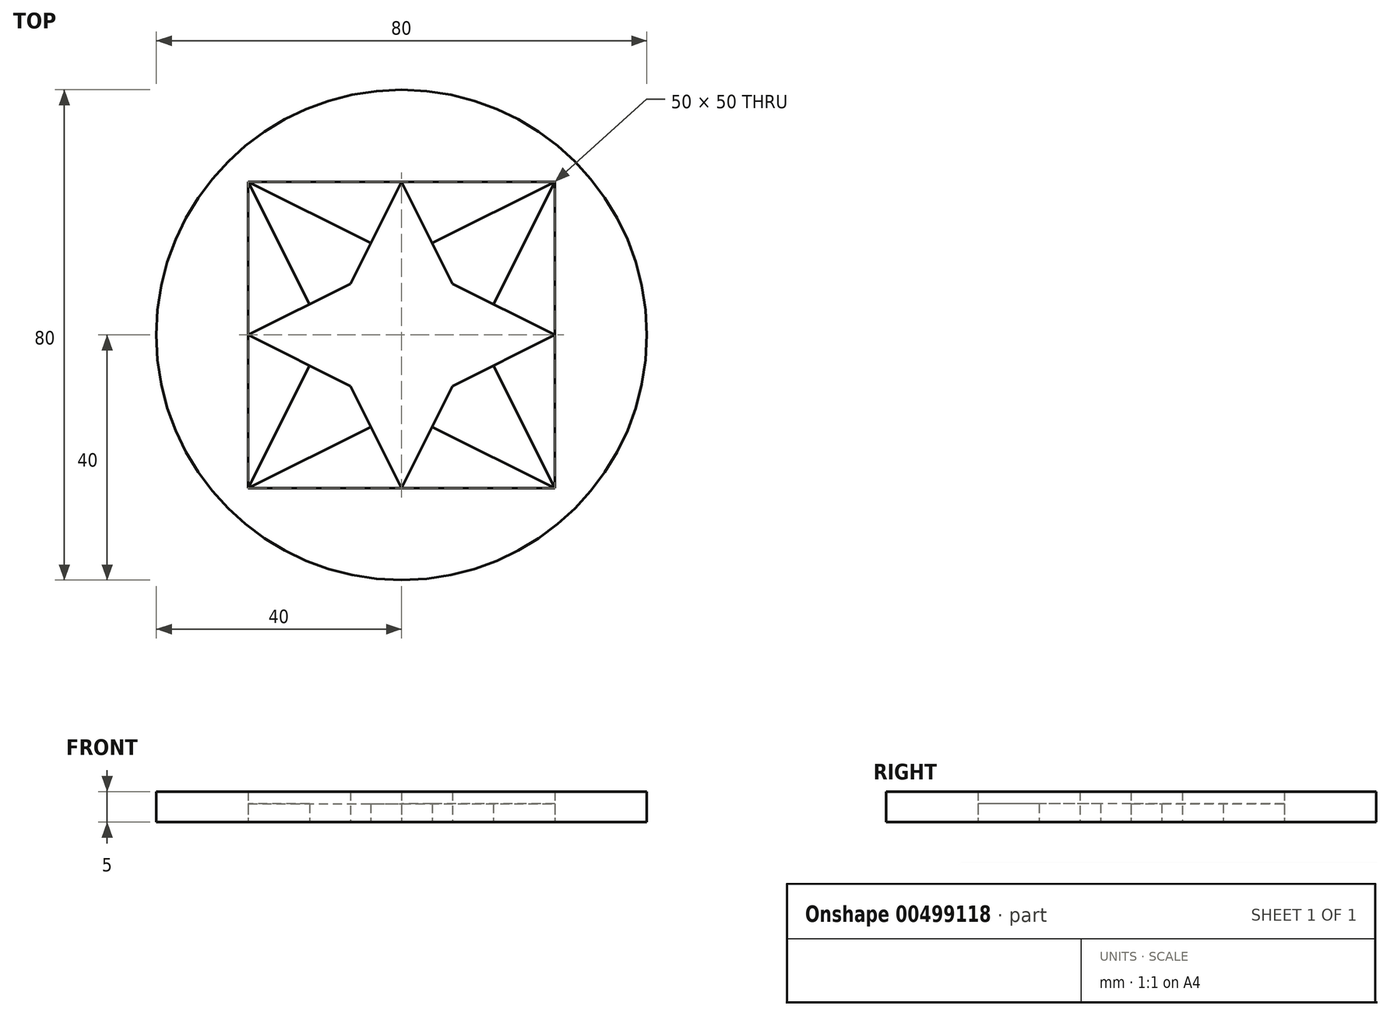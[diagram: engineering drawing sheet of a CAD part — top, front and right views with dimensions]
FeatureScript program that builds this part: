
annotation { "Feature Type Name" : "Feature", "Feature Type Description" : "" }
export const myFeature = defineFeature(function(context is Context, id is Id, definition is map)
    precondition{}
    {
        {
            var Q0;
            Q0=qCreatedBy(makeId("Top.planeOp"),FACE);
            var sketch = newSketch(context, id + "F0", { "sketchPlane" : qUnion([Q0])});
            skCircle(sketch, "E0", {"center": v(0, 0) * mm, "radius": 40 * mm});
            skLineSegment(sketch, "E1.bottom", {"start": v(-25, 25) * mm, "end": v(25, 25) * mm});
            skLineSegment(sketch, "E1.top", {"start": v(-25, -25) * mm, "end": v(25, -25) * mm});
            skLineSegment(sketch, "E1.left", {"start": v(-25, 25) * mm, "end": v(-25, -25) * mm});
            skLineSegment(sketch, "E1.right", {"start": v(25, 25) * mm, "end": v(25, -25) * mm});
            skLineSegment(sketch, "E2", {"start": v(-25, 25) * mm, "end": v(25, 0) * mm});
            skLineSegment(sketch, "E3", {"start": v(25, 0) * mm, "end": v(-25, -25) * mm});
            skLineSegment(sketch, "E4", {"start": v(-25, -25) * mm, "end": v(0, 25) * mm});
            skLineSegment(sketch, "E5", {"start": v(0, 25) * mm, "end": v(25, -25) * mm});
            skLineSegment(sketch, "E6", {"start": v(25, -25) * mm, "end": v(-25, 0) * mm});
            skLineSegment(sketch, "E7", {"start": v(-25, 0) * mm, "end": v(25, 25) * mm});
            skLineSegment(sketch, "E8", {"start": v(25, 25) * mm, "end": v(0, -25) * mm});
            skLineSegment(sketch, "E9", {"start": v(0, -25) * mm, "end": v(-25, 25) * mm});
            skSolve(sketch);
        }
        {
            var Q0;
            Q0=makeQuery(id+"F0.imprint","IMPRINT",FACE,{"disambiguationData":[TD([[makeQuery(id+"F0.imprint","IMPRINT",EDGE,{"derivedFrom":sQuery(id+"F0.wireOp",EDGE,"E0")}),1.0]])]});
            var Q1;
            {var subQ0=sQuery(id+"F0.wireOp",EDGE,"E6");var subQ1=sQuery(id+"F0.wireOp",EDGE,"E4");var subQ2=makeQuery(id+"F0.imprint","INTERSECT",VERTEX,{"derivedFrom":[subQ1,subQ0]});Q1=makeQuery(id+"F0.imprint","IMPRINT",FACE,{"disambiguationData":[TD([[makeQuery(id+"F0.imprint","IMPRINT",EDGE,{"disambiguationData":[TD([[subQ2,-1.0]])],"derivedFrom":subQ1}),1.0]])]});}
            var Q2;
            {var subQ0=sQuery(id+"F0.wireOp",EDGE,"E3");var subQ5=sQuery(id+"F0.wireOp",EDGE,"E5");var subQ6=makeQuery(id+"F0.imprint","INTERSECT",VERTEX,{"derivedFrom":[subQ0,subQ5]});Q2=makeQuery(id+"F0.imprint","IMPRINT",FACE,{"disambiguationData":[TD([[makeQuery(id+"F0.imprint","IMPRINT",EDGE,{"disambiguationData":[TD([[subQ6,1.0]])],"derivedFrom":subQ5}),1.0]])]});}
            var Q3;
            {var subQ0=sQuery(id+"F0.wireOp",EDGE,"E4");var subQ1=sQuery(id+"F0.wireOp",EDGE,"E2");var subQ2=makeQuery(id+"F0.imprint","INTERSECT",VERTEX,{"derivedFrom":[subQ1,subQ0]});Q3=makeQuery(id+"F0.imprint","IMPRINT",FACE,{"disambiguationData":[TD([[makeQuery(id+"F0.imprint","IMPRINT",EDGE,{"disambiguationData":[TD([[subQ2,-1.0]])],"derivedFrom":subQ1}),1.0]])]});}
            var Q4;
            {var subQ0=sQuery(id+"F0.wireOp",EDGE,"E6");var subQ1=sQuery(id+"F0.wireOp",EDGE,"E3");var subQ2=makeQuery(id+"F0.imprint","INTERSECT",VERTEX,{"derivedFrom":[subQ1,subQ0]});Q4=makeQuery(id+"F0.imprint","IMPRINT",FACE,{"disambiguationData":[TD([[makeQuery(id+"F0.imprint","IMPRINT",EDGE,{"disambiguationData":[TD([[subQ2,-1.0]])],"derivedFrom":subQ1}),1.0]])]});}
            var Q5;
            {var subQ1=sQuery(id+"F0.wireOp",EDGE,"E2");var subQ8=sQuery(id+"F0.wireOp",EDGE,"E7");var subQ14=makeQuery(id+"F0.imprint","INTERSECT",VERTEX,{"derivedFrom":[subQ1,subQ8]});Q5=makeQuery(id+"F0.imprint","IMPRINT",FACE,{"disambiguationData":[TD([[makeQuery(id+"F0.imprint","IMPRINT",EDGE,{"disambiguationData":[TD([[subQ14,-1.0]])],"derivedFrom":subQ1}),-1.0]])]});}
            var Q6;
            {var subQ0=sQuery(id+"F0.wireOp",EDGE,"E9");var subQ1=sQuery(id+"F0.wireOp",EDGE,"E4");var subQ2=makeQuery(id+"F0.imprint","INTERSECT",VERTEX,{"derivedFrom":[subQ1,subQ0]});Q6=makeQuery(id+"F0.imprint","IMPRINT",FACE,{"disambiguationData":[TD([[makeQuery(id+"F0.imprint","IMPRINT",EDGE,{"disambiguationData":[TD([[subQ2,-1.0]])],"derivedFrom":subQ1}),1.0]])]});}
            var Q7;
            {var subQ0=sQuery(id+"F0.wireOp",EDGE,"E6");var subQ1=sQuery(id+"F0.wireOp",EDGE,"E4");var subQ2=makeQuery(id+"F0.imprint","INTERSECT",VERTEX,{"derivedFrom":[subQ1,subQ0]});Q7=makeQuery(id+"F0.imprint","IMPRINT",FACE,{"disambiguationData":[TD([[makeQuery(id+"F0.imprint","IMPRINT",EDGE,{"disambiguationData":[TD([[subQ2,-1.0]])],"derivedFrom":subQ1}),-1.0]])]});}
            var Q8;
            {var subQ0=sQuery(id+"F0.wireOp",EDGE,"E6");var subQ1=sQuery(id+"F0.wireOp",EDGE,"E3");var subQ2=makeQuery(id+"F0.imprint","INTERSECT",VERTEX,{"derivedFrom":[subQ1,subQ0]});Q8=makeQuery(id+"F0.imprint","IMPRINT",FACE,{"disambiguationData":[TD([[makeQuery(id+"F0.imprint","IMPRINT",EDGE,{"disambiguationData":[TD([[subQ2,-1.0]])],"derivedFrom":subQ1}),-1.0]])]});}
            var Q9;
            {var subQ0=sQuery(id+"F0.wireOp",EDGE,"E8");var subQ1=sQuery(id+"F0.wireOp",EDGE,"E3");var subQ2=makeQuery(id+"F0.imprint","INTERSECT",VERTEX,{"derivedFrom":[subQ1,subQ0]});Q9=makeQuery(id+"F0.imprint","IMPRINT",FACE,{"disambiguationData":[TD([[makeQuery(id+"F0.imprint","IMPRINT",EDGE,{"disambiguationData":[TD([[subQ2,-1.0]])],"derivedFrom":subQ1}),1.0]])]});}
            var Q10;
            {var subQ0=sQuery(id+"F0.wireOp",EDGE,"E5");var subQ1=sQuery(id+"F0.wireOp",EDGE,"E3");var subQ2=makeQuery(id+"F0.imprint","INTERSECT",VERTEX,{"derivedFrom":[subQ1,subQ0]});Q10=makeQuery(id+"F0.imprint","IMPRINT",FACE,{"disambiguationData":[TD([[makeQuery(id+"F0.imprint","IMPRINT",EDGE,{"disambiguationData":[TD([[subQ2,-1.0]])],"derivedFrom":subQ1}),-1.0]])]});}
            var Q11;
            {var subQ0=sQuery(id+"F0.wireOp",EDGE,"E5");var subQ1=sQuery(id+"F0.wireOp",EDGE,"E2");var subQ2=makeQuery(id+"F0.imprint","INTERSECT",VERTEX,{"derivedFrom":[subQ1,subQ0]});Q11=makeQuery(id+"F0.imprint","IMPRINT",FACE,{"disambiguationData":[TD([[makeQuery(id+"F0.imprint","IMPRINT",EDGE,{"disambiguationData":[TD([[subQ2,-1.0]])],"derivedFrom":subQ1}),-1.0]])]});}
            var Q12;
            {var subQ0=sQuery(id+"F0.wireOp",EDGE,"E7");var subQ1=sQuery(id+"F0.wireOp",EDGE,"E2");var subQ2=makeQuery(id+"F0.imprint","INTERSECT",VERTEX,{"derivedFrom":[subQ1,subQ0]});Q12=makeQuery(id+"F0.imprint","IMPRINT",FACE,{"disambiguationData":[TD([[makeQuery(id+"F0.imprint","IMPRINT",EDGE,{"disambiguationData":[TD([[subQ2,-1.0]])],"derivedFrom":subQ1}),1.0]])]});}
            var Q13;
            {var subQ0=sQuery(id+"F0.wireOp",EDGE,"E4");var subQ1=sQuery(id+"F0.wireOp",EDGE,"E2");var subQ2=makeQuery(id+"F0.imprint","INTERSECT",VERTEX,{"derivedFrom":[subQ1,subQ0]});Q13=makeQuery(id+"F0.imprint","IMPRINT",FACE,{"disambiguationData":[TD([[makeQuery(id+"F0.imprint","IMPRINT",EDGE,{"disambiguationData":[TD([[subQ2,-1.0]])],"derivedFrom":subQ1}),-1.0]])]});}
            extrude(context, id + "F1", {"entities" : qUnion([Q0, Q1, Q2, Q3, Q4, Q5, Q6, Q7, Q8, Q9, Q10, Q11, Q12, Q13]), "depth" : 5 * mm});
        }
        {
            var Q0;
            {var subQ0=sQuery(id+"F0.wireOp",EDGE,"E9");var subQ3=sQuery(id+"F0.wireOp",EDGE,"E7");var subQ5=makeQuery(id+"F0.imprint","INTERSECT",VERTEX,{"derivedFrom":[subQ3,subQ0]});Q0=makeQuery(id+"F0.imprint","IMPRINT",FACE,{"disambiguationData":[TD([[makeQuery(id+"F0.imprint","IMPRINT",EDGE,{"disambiguationData":[TD([[subQ5,1.0]])],"derivedFrom":subQ3}),1.0]])]});}
            var Q1;
            {var subQ0=sQuery(id+"F0.wireOp",EDGE,"E2");var subQ3=sQuery(id+"F0.wireOp",EDGE,"E4");var subQ5=makeQuery(id+"F0.imprint","INTERSECT",VERTEX,{"derivedFrom":[subQ0,subQ3]});Q1=makeQuery(id+"F0.imprint","IMPRINT",FACE,{"disambiguationData":[TD([[makeQuery(id+"F0.imprint","IMPRINT",EDGE,{"disambiguationData":[TD([[subQ5,-1.0]])],"derivedFrom":subQ3}),1.0]])]});}
            var Q2;
            {var subQ0=sQuery(id+"F0.wireOp",EDGE,"E7");var subQ3=sQuery(id+"F0.wireOp",EDGE,"E5");var subQ5=makeQuery(id+"F0.imprint","INTERSECT",VERTEX,{"derivedFrom":[subQ3,subQ0]});Q2=makeQuery(id+"F0.imprint","IMPRINT",FACE,{"disambiguationData":[TD([[makeQuery(id+"F0.imprint","IMPRINT",EDGE,{"disambiguationData":[TD([[subQ5,1.0]])],"derivedFrom":subQ3}),1.0]])]});}
            var Q3;
            {var subQ0=sQuery(id+"F0.wireOp",EDGE,"E8");var subQ3=sQuery(id+"F0.wireOp",EDGE,"E2");var subQ5=makeQuery(id+"F0.imprint","INTERSECT",VERTEX,{"derivedFrom":[subQ3,subQ0]});Q3=makeQuery(id+"F0.imprint","IMPRINT",FACE,{"disambiguationData":[TD([[makeQuery(id+"F0.imprint","IMPRINT",EDGE,{"disambiguationData":[TD([[subQ5,-1.0]])],"derivedFrom":subQ3}),1.0]])]});}
            var Q4;
            {var subQ0=sQuery(id+"F0.wireOp",EDGE,"E5");var subQ3=sQuery(id+"F0.wireOp",EDGE,"E3");var subQ5=makeQuery(id+"F0.imprint","INTERSECT",VERTEX,{"derivedFrom":[subQ3,subQ0]});Q4=makeQuery(id+"F0.imprint","IMPRINT",FACE,{"disambiguationData":[TD([[makeQuery(id+"F0.imprint","IMPRINT",EDGE,{"disambiguationData":[TD([[subQ5,1.0]])],"derivedFrom":subQ3}),1.0]])]});}
            var Q5;
            {var subQ0=sQuery(id+"F0.wireOp",EDGE,"E6");var subQ3=sQuery(id+"F0.wireOp",EDGE,"E8");var subQ5=makeQuery(id+"F0.imprint","INTERSECT",VERTEX,{"derivedFrom":[subQ0,subQ3]});Q5=makeQuery(id+"F0.imprint","IMPRINT",FACE,{"disambiguationData":[TD([[makeQuery(id+"F0.imprint","IMPRINT",EDGE,{"disambiguationData":[TD([[subQ5,-1.0]])],"derivedFrom":subQ3}),1.0]])]});}
            var Q6;
            {var subQ0=sQuery(id+"F0.wireOp",EDGE,"E3");var subQ3=sQuery(id+"F0.wireOp",EDGE,"E9");var subQ5=makeQuery(id+"F0.imprint","INTERSECT",VERTEX,{"derivedFrom":[subQ0,subQ3]});Q6=makeQuery(id+"F0.imprint","IMPRINT",FACE,{"disambiguationData":[TD([[makeQuery(id+"F0.imprint","IMPRINT",EDGE,{"disambiguationData":[TD([[subQ5,1.0]])],"derivedFrom":subQ3}),1.0]])]});}
            var Q7;
            {var subQ0=sQuery(id+"F0.wireOp",EDGE,"E4");var subQ3=sQuery(id+"F0.wireOp",EDGE,"E6");var subQ5=makeQuery(id+"F0.imprint","INTERSECT",VERTEX,{"derivedFrom":[subQ0,subQ3]});Q7=makeQuery(id+"F0.imprint","IMPRINT",FACE,{"disambiguationData":[TD([[makeQuery(id+"F0.imprint","IMPRINT",EDGE,{"disambiguationData":[TD([[subQ5,-1.0]])],"derivedFrom":subQ3}),1.0]])]});}
            extrude(context, id + "F2", {"entities" : qUnion([Q0, Q1, Q2, Q3, Q4, Q5, Q6, Q7]), "depth" : 3 * mm});
        }
    });
